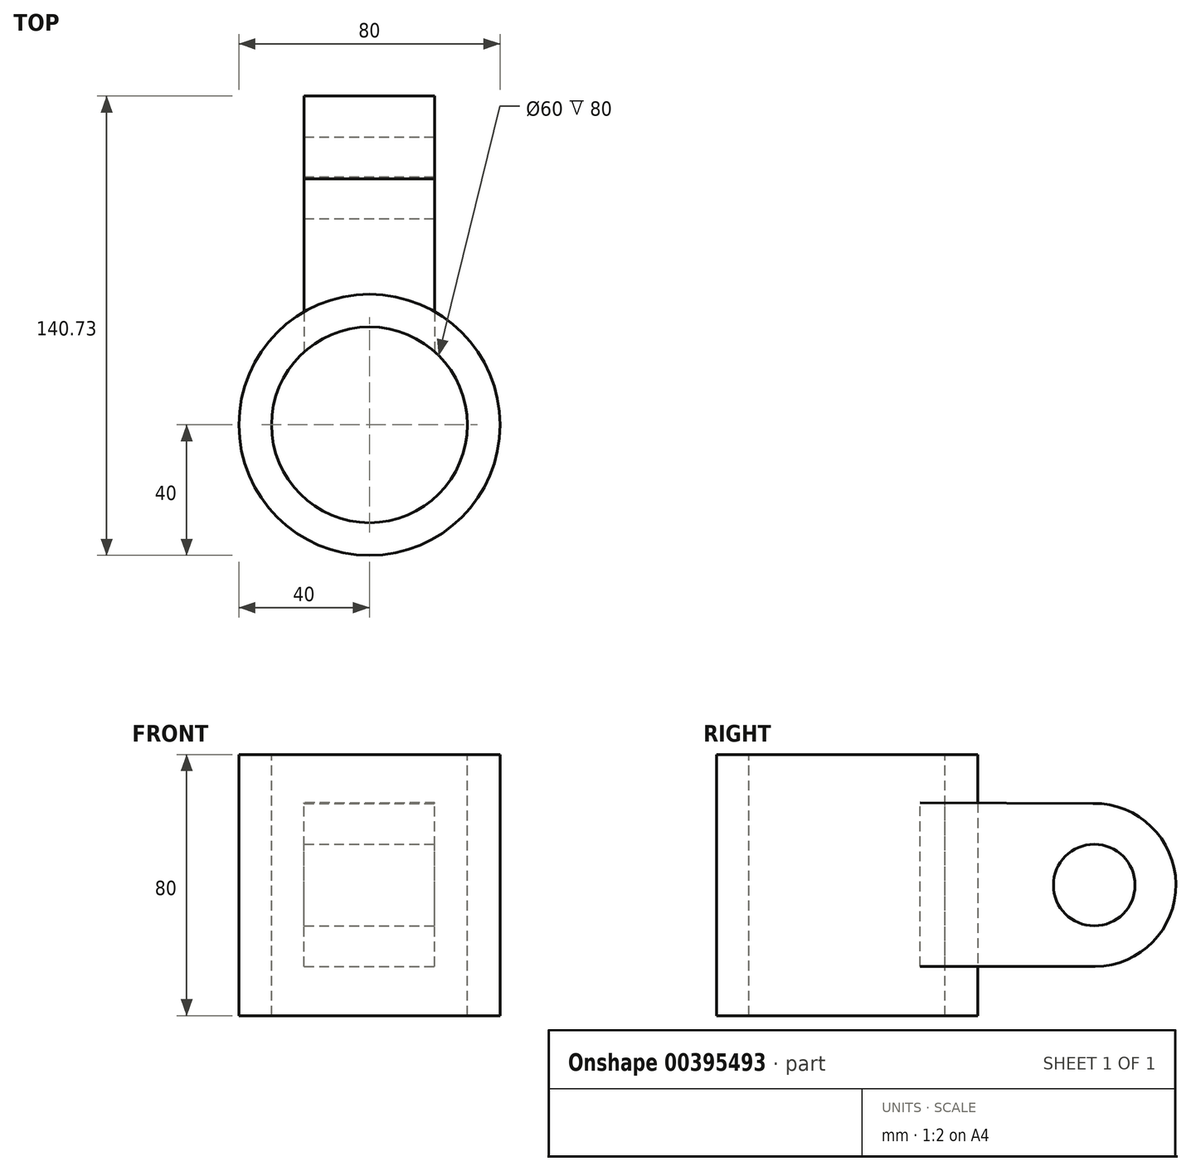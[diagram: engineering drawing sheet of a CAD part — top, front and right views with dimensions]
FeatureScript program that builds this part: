
annotation { "Feature Type Name" : "Feature", "Feature Type Description" : "" }
export const myFeature = defineFeature(function(context is Context, id is Id, definition is map)
    precondition{}
    {
        {
            var Q0;
            Q0=qCreatedBy(makeId("Top.planeOp"),FACE);
            var sketch = newSketch(context, id + "F0", { "sketchPlane" : qUnion([Q0])});
            skCircle(sketch, "E0", {"center": v(0, 0) * mm, "radius": 40 * mm});
            skSolve(sketch);
        }
        {
            var Q0;
            Q0 = qSketchRegion(id + "F0", true);
            extrude(context, id + "F1", {"entities" : qUnion([Q0]), "depth" : 80 * mm});
        }
        {
            var Q0;
            Q0=qCreatedBy(makeId("Right.planeOp"),FACE);
            var sketch = newSketch(context, id + "F2", { "sketchPlane" : qUnion([Q0])});
            skLineSegment(sketch, "E1.0.1", {"start": v(14.46, 15.12) * mm, "end": v(76.05, 15) * mm});
            skArc(sketch, "E1.0.2", {"start": v(76.05, 15) * mm, "mid": v(100.73, 40.32) * mm, "end": v(75.4, 65) * mm});
            skLineSegment(sketch, "E1.0.3", {"start": v(75.4, 65) * mm, "end": v(14.46, 65.2) * mm});
            skCircle(sketch, "E2", {"center": v(75.73, 40) * mm, "radius": 12.5 * mm});
            skPoint(sketch, "E1.0.0.end.orphan", {"position": v(33.82, 65.14) * mm});
            skLineSegment(sketch, "E3", {"start": v(14.46, 65.2) * mm, "end": v(14.46, 15.12) * mm});
            skSolve(sketch);
        }
        {
            var Q0;
            Q0=makeQuery(id+"F2.imprint","IMPRINT",FACE,{"disambiguationData":[TD([[makeQuery(id+"F2.imprint","IMPRINT",EDGE,{"derivedFrom":sQuery(id+"F2.wireOp",EDGE,"E1.0.1")}),1.0]])]});
            extrude(context, id + "F3", {"entities" : qUnion([Q0]), "oppositeDirection" : true, "depth" : 20 * mm, "hasSecondDirection" : true, "secondDirectionOppositeDirection" : false, "secondDirectionDepth" : 20 * mm});
        }
        {
            var Q0;
            Q0=makeQuery(id+"F1.opExtrude","CAP_FACE",FACE,{"disambiguationData":[OSD([sQuery(id+"F0.wireOp",EDGE,"E0")])],"isStart":false});
            var sketch = newSketch(context, id + "F4", { "sketchPlane" : qUnion([Q0])});
            skCircle(sketch, "E4", {"center": v(0, 0) * mm, "radius": 30 * mm});
            skSolve(sketch);
        }
        {
            var Q0;
            Q0=makeQuery(id+"F4.imprint","IMPRINT",FACE,{"disambiguationData":[TD([[makeQuery(id+"F4.imprint","IMPRINT",EDGE,{"derivedFrom":sQuery(id+"F4.wireOp",EDGE,"E4")}),1.0]])]});
            extrude(context, id + "F5", {"entities" : qUnion([Q0]), "operationType" : NewBodyOperationType.REMOVE, "oppositeDirection" : true, "depth" : 146 * mm});
        }
    });
